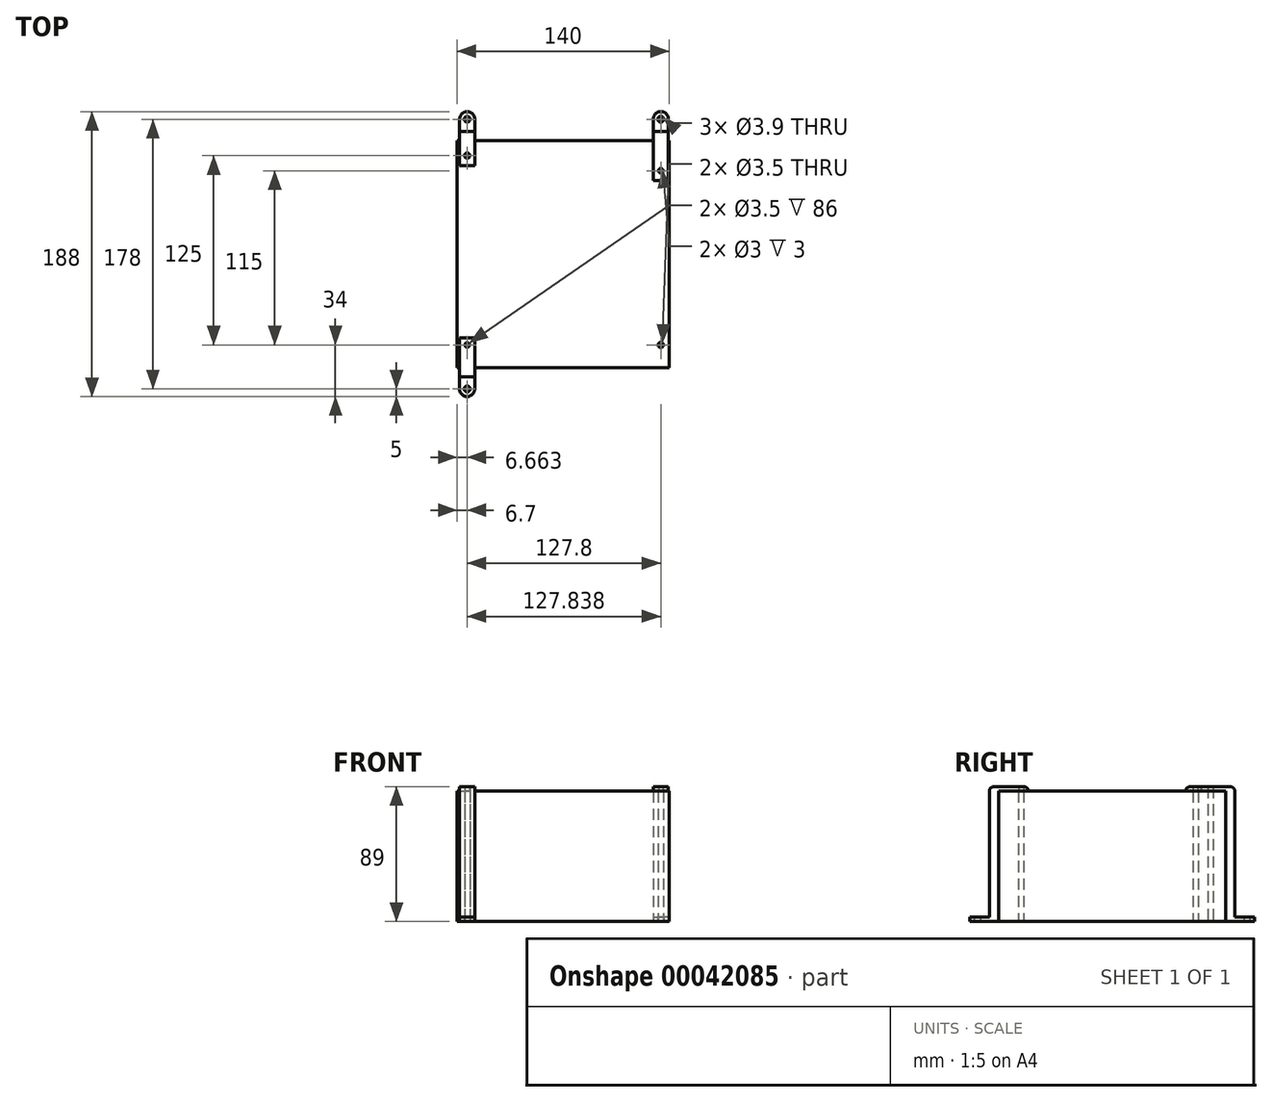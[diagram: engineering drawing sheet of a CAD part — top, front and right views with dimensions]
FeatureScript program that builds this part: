
annotation { "Feature Type Name" : "Feature", "Feature Type Description" : "" }
export const myFeature = defineFeature(function(context is Context, id is Id, definition is map)
    precondition{}
    {
        {
            var Q0;
            Q0=qCreatedBy(makeId("Top.planeOp"),FACE);
            var sketch = newSketch(context, id + "F0", { "sketchPlane" : qUnion([Q0])});
            skLineSegment(sketch, "E0.rect.bottom", {"start": v(70, -75) * mm, "end": v(-70, -75) * mm});
            skLineSegment(sketch, "E0.rect.top", {"start": v(70, 75) * mm, "end": v(-70, 75) * mm});
            skLineSegment(sketch, "E0.rect.left", {"start": v(70, -75) * mm, "end": v(70, 75) * mm});
            skLineSegment(sketch, "E0.rect.right", {"start": v(-70, -75) * mm, "end": v(-70, 75) * mm});
            skPoint(sketch, "E0.rect.middle", {"position": v(0, 0) * mm});
            skCircle(sketch, "E1", {"center": v(-63.3, 65) * mm, "radius": 1.75 * mm});
            skCircle(sketch, "E2", {"center": v(64.5, 55) * mm, "radius": 1.75 * mm});
            skCircle(sketch, "E3", {"center": v(64.5, -60) * mm, "radius": 1.75 * mm});
            skCircle(sketch, "E4", {"center": v(-63.3, -60) * mm, "radius": 1.75 * mm});
            skSolve(sketch);
        }
        {
            var Q0;
            Q0 = qSketchRegion(id + "F0", true);
            extrude(context, id + "F1", {"entities" : qUnion([Q0]), "depth" : 86 * mm});
        }
        {
            var Q0;
            Q0=qCreatedBy(makeId("Top.planeOp"),FACE);
            var sketch = newSketch(context, id + "F2", { "sketchPlane" : qUnion([Q0])});
            skCircle(sketch, "E5", {"center": v(-63.3, 89) * mm, "radius": 1.95 * mm});
            skCircle(sketch, "E6", {"center": v(-63.3, 89) * mm, "radius": 5 * mm});
            skLineSegment(sketch, "E7.bottom", {"start": v(-68.3, 75) * mm, "end": v(-58.3, 75) * mm});
            skLineSegment(sketch, "E7.top", {"start": v(-68.3, 81) * mm, "end": v(-58.3, 81) * mm});
            skLineSegment(sketch, "E7.left", {"start": v(-68.3, 75) * mm, "end": v(-68.3, 81) * mm});
            skLineSegment(sketch, "E7.right", {"start": v(-58.3, 75) * mm, "end": v(-58.3, 81) * mm});
            skLineSegment(sketch, "E8", {"start": v(-63.3, 98.83) * mm, "end": v(-63.3, 65) * mm, "construction": true});
            skLineSegment(sketch, "E9", {"start": v(-68.3, 81) * mm, "end": v(-68.3, 89) * mm});
            skLineSegment(sketch, "E10", {"start": v(-58.3, 81) * mm, "end": v(-58.3, 89) * mm});
            skSolve(sketch);
        }
        {
            var Q0;
            Q0=makeQuery(id+"F2.imprint","IMPRINT",FACE,{"disambiguationData":[TD([[makeQuery(id+"F2.imprint","IMPRINT",EDGE,{"derivedFrom":sQuery(id+"F2.wireOp",EDGE,"E5")}),-1.0]])]});
            var Q1;
            Q1=makeQuery(id+"F2.imprint","IMPRINT",FACE,{"disambiguationData":[TD([[makeQuery(id+"F2.imprint","IMPRINT",EDGE,{"derivedFrom":sQuery(id+"F2.wireOp",EDGE,"E7.top")}),1.0]])]});
            extrude(context, id + "F3", {"entities" : qUnion([Q0, Q1]), "depth" : 3 * mm});
        }
        {
            var Q0;
            Q0=makeQuery(id+"F2.imprint","IMPRINT",FACE,{"disambiguationData":[TD([[makeQuery(id+"F2.imprint","IMPRINT",EDGE,{"derivedFrom":sQuery(id+"F2.wireOp",EDGE,"E7.bottom")}),1.0]])]});
            extrude(context, id + "F4", {"entities" : qUnion([Q0]), "operationType" : NewBodyOperationType.ADD, "depth" : 86 * mm});
        }
        {
            var Q0;
            Q0=makeQuery(id+"F4.opExtrude","CAP_FACE",FACE,{"disambiguationData":[OSD([sQuery(id+"F2.wireOp",EDGE,"E7.bottom"),sQuery(id+"F2.wireOp",EDGE,"E7.top"),sQuery(id+"F2.wireOp",EDGE,"E7.left"),sQuery(id+"F2.wireOp",EDGE,"E7.right")])],"isStart":false});
            var sketch = newSketch(context, id + "F5", { "sketchPlane" : qUnion([Q0])});
            skLineSegment(sketch, "E11.bottom", {"start": v(-68.3, 81) * mm, "end": v(-58.3, 81) * mm});
            skLineSegment(sketch, "E11.top", {"start": v(-68.3, 58.38) * mm, "end": v(-58.3, 58.38) * mm});
            skLineSegment(sketch, "E11.left", {"start": v(-68.3, 81) * mm, "end": v(-68.3, 58.38) * mm});
            skLineSegment(sketch, "E11.right", {"start": v(-58.3, 81) * mm, "end": v(-58.3, 58.38) * mm});
            skCircle(sketch, "E12", {"center": v(-63.3, 65) * mm, "radius": 1.5 * mm});
            skSolve(sketch);
        }
        {
            var Q0;
            {var subQ2=sQuery(id+"F5.wireOp",EDGE,"E11.top");Q0=makeQuery(id+"F5.imprint","IMPRINT",FACE,{"disambiguationData":[TD([[makeQuery(id+"F5.imprint","IMPRINT",EDGE,{"derivedFrom":subQ2}),1.0]])]});}
            var Q1;
            {var subQ2=sQuery(id+"F5.wireOp",EDGE,"E11.bottom");Q1=makeQuery(id+"F5.imprint","IMPRINT",FACE,{"disambiguationData":[TD([[makeQuery(id+"F5.imprint","IMPRINT",EDGE,{"derivedFrom":subQ2}),-1.0]])]});}
            extrude(context, id + "F6", {"entities" : qUnion([Q0, Q1]), "operationType" : NewBodyOperationType.ADD, "depth" : 3 * mm});
        }
        {
            var Q0;
            Q0=qCreatedBy(makeId("Top.planeOp"),FACE);
            var sketch = newSketch(context, id + "F7", { "sketchPlane" : qUnion([Q0])});
            skCircle(sketch, "E13", {"center": v(64.5, 89) * mm, "radius": 1.95 * mm});
            skCircle(sketch, "E14", {"center": v(64.5, 89) * mm, "radius": 5 * mm});
            skLineSegment(sketch, "E15.bottom", {"start": v(59.5, 75) * mm, "end": v(69.5, 75) * mm});
            skLineSegment(sketch, "E15.top", {"start": v(59.5, 81) * mm, "end": v(69.5, 81) * mm});
            skLineSegment(sketch, "E15.left", {"start": v(59.5, 75) * mm, "end": v(59.5, 81) * mm});
            skLineSegment(sketch, "E15.right", {"start": v(69.5, 75) * mm, "end": v(69.5, 81) * mm});
            skLineSegment(sketch, "E16", {"start": v(64.5, 98.83) * mm, "end": v(64.5, 65) * mm, "construction": true});
            skLineSegment(sketch, "E17", {"start": v(59.5, 81) * mm, "end": v(59.5, 89) * mm});
            skLineSegment(sketch, "E18", {"start": v(69.5, 81) * mm, "end": v(69.5, 89) * mm});
            skSolve(sketch);
        }
        {
            var Q0;
            Q0=makeQuery(id+"F7.imprint","IMPRINT",FACE,{"disambiguationData":[TD([[makeQuery(id+"F7.imprint","IMPRINT",EDGE,{"derivedFrom":sQuery(id+"F7.wireOp",EDGE,"E13")}),-1.0]])]});
            var Q1;
            Q1=makeQuery(id+"F7.imprint","IMPRINT",FACE,{"disambiguationData":[TD([[makeQuery(id+"F7.imprint","IMPRINT",EDGE,{"derivedFrom":sQuery(id+"F7.wireOp",EDGE,"E15.top")}),1.0]])]});
            extrude(context, id + "F8", {"entities" : qUnion([Q0, Q1]), "depth" : 3 * mm});
        }
        {
            var Q0;
            Q0=makeQuery(id+"F7.imprint","IMPRINT",FACE,{"disambiguationData":[TD([[makeQuery(id+"F7.imprint","IMPRINT",EDGE,{"derivedFrom":sQuery(id+"F7.wireOp",EDGE,"E15.bottom")}),1.0]])]});
            extrude(context, id + "F9", {"entities" : qUnion([Q0]), "operationType" : NewBodyOperationType.ADD, "depth" : 86 * mm});
        }
        {
            var Q0;
            Q0=makeQuery(id+"F9.opExtrude","CAP_FACE",FACE,{"disambiguationData":[OSD([sQuery(id+"F7.wireOp",EDGE,"E15.bottom"),sQuery(id+"F7.wireOp",EDGE,"E15.top"),sQuery(id+"F7.wireOp",EDGE,"E15.left"),sQuery(id+"F7.wireOp",EDGE,"E15.right")])],"isStart":false});
            var sketch = newSketch(context, id + "F10", { "sketchPlane" : qUnion([Q0])});
            skLineSegment(sketch, "E19.bottom", {"start": v(59.5, 81) * mm, "end": v(69.5, 81) * mm});
            skLineSegment(sketch, "E19.top", {"start": v(59.5, 48.52) * mm, "end": v(69.5, 48.52) * mm});
            skLineSegment(sketch, "E19.left", {"start": v(59.5, 81) * mm, "end": v(59.5, 48.52) * mm});
            skLineSegment(sketch, "E19.right", {"start": v(69.5, 81) * mm, "end": v(69.5, 48.52) * mm});
            skCircle(sketch, "E20", {"center": v(64.5, 55) * mm, "radius": 1.5 * mm});
            skSolve(sketch);
        }
        {
            var Q0;
            Q0 = qSketchRegion(id + "F10", true);
            extrude(context, id + "F11", {"entities" : qUnion([Q0]), "operationType" : NewBodyOperationType.ADD, "depth" : 3 * mm});
        }
        {
            var Q0;
            Q0=qCreatedBy(makeId("Top.planeOp"),FACE);
            var sketch = newSketch(context, id + "F12", { "sketchPlane" : qUnion([Q0])});
            skCircle(sketch, "E21", {"center": v(-63.34, -89) * mm, "radius": 1.95 * mm});
            skCircle(sketch, "E22", {"center": v(-63.34, -89) * mm, "radius": 5 * mm});
            skLineSegment(sketch, "E23.bottom", {"start": v(-68.34, -75) * mm, "end": v(-58.34, -75) * mm});
            skLineSegment(sketch, "E23.top", {"start": v(-68.34, -81) * mm, "end": v(-58.34, -81) * mm});
            skLineSegment(sketch, "E23.left", {"start": v(-68.34, -81) * mm, "end": v(-68.34, -75) * mm});
            skLineSegment(sketch, "E23.right", {"start": v(-58.34, -81) * mm, "end": v(-58.34, -75) * mm});
            skLineSegment(sketch, "E24", {"start": v(-63.34, -31.67) * mm, "end": v(-63.34, -61.75) * mm, "construction": true});
            skLineSegment(sketch, "E25", {"start": v(-68.34, -89) * mm, "end": v(-68.34, -81) * mm});
            skLineSegment(sketch, "E26", {"start": v(-58.34, -89) * mm, "end": v(-58.34, -81) * mm});
            skSolve(sketch);
        }
        {
            var Q0;
            Q0=makeQuery(id+"F12.imprint","IMPRINT",FACE,{"disambiguationData":[TD([[makeQuery(id+"F12.imprint","IMPRINT",EDGE,{"derivedFrom":sQuery(id+"F12.wireOp",EDGE,"E23.bottom")}),-1.0]])]});
            extrude(context, id + "F13", {"entities" : qUnion([Q0]), "depth" : 86 * mm});
        }
        {
            var Q0;
            Q0=makeQuery(id+"F12.imprint","IMPRINT",FACE,{"disambiguationData":[TD([[makeQuery(id+"F12.imprint","IMPRINT",EDGE,{"derivedFrom":sQuery(id+"F12.wireOp",EDGE,"E23.top")}),-1.0]])]});
            var Q1;
            Q1=makeQuery(id+"F12.imprint","IMPRINT",FACE,{"disambiguationData":[TD([[makeQuery(id+"F12.imprint","IMPRINT",EDGE,{"derivedFrom":sQuery(id+"F12.wireOp",EDGE,"E21")}),-1.0]])]});
            extrude(context, id + "F14", {"entities" : qUnion([Q0, Q1]), "operationType" : NewBodyOperationType.ADD, "depth" : 3 * mm});
        }
        {
            var Q0;
            Q0=makeQuery(id+"F13.opExtrude","CAP_FACE",FACE,{"disambiguationData":[OSD([sQuery(id+"F12.wireOp",EDGE,"E23.bottom"),sQuery(id+"F12.wireOp",EDGE,"E23.top"),sQuery(id+"F12.wireOp",EDGE,"E23.left"),sQuery(id+"F12.wireOp",EDGE,"E23.right")])],"isStart":false});
            var sketch = newSketch(context, id + "F15", { "sketchPlane" : qUnion([Q0])});
            skLineSegment(sketch, "E27.bottom", {"start": v(-68.34, -55.23) * mm, "end": v(-58.34, -55.23) * mm});
            skLineSegment(sketch, "E27.top", {"start": v(-68.34, -81) * mm, "end": v(-58.34, -81) * mm});
            skLineSegment(sketch, "E27.left", {"start": v(-68.34, -55.23) * mm, "end": v(-68.34, -81) * mm});
            skLineSegment(sketch, "E27.right", {"start": v(-58.34, -55.23) * mm, "end": v(-58.34, -81) * mm});
            skCircle(sketch, "E28", {"center": v(-63.3, -60) * mm, "radius": 1.5 * mm});
            skSolve(sketch);
        }
        {
            var Q0;
            Q0 = qSketchRegion(id + "F15", true);
            extrude(context, id + "F16", {"entities" : qUnion([Q0]), "operationType" : NewBodyOperationType.ADD, "depth" : 3 * mm});
        }
        {
            var Q0;
            Q0=makeQuery(id+"F11.opExtrude","CAP_EDGE",EDGE,{"disambiguationData":[OSD([sQuery(id+"F10.wireOp",EDGE,"E19.bottom")])],"isStart":false});
            var Q1;
            Q1=makeQuery(id+"F6.opExtrude","CAP_EDGE",EDGE,{"disambiguationData":[OSD([sQuery(id+"F5.wireOp",EDGE,"E11.bottom")])],"isStart":false});
            var Q2;
            Q2=makeQuery(id+"F8.opExtrude","CAP_EDGE",EDGE,{"disambiguationData":[OSD([sQuery(id+"F7.wireOp",EDGE,"E15.top")])],"isStart":false});
            var Q3;
            Q3=makeQuery(id+"F3.opExtrude","CAP_EDGE",EDGE,{"disambiguationData":[OSD([sQuery(id+"F2.wireOp",EDGE,"E7.top")])],"isStart":false});
            var Q4;
            Q4=makeQuery(id+"F11.opExtrude","CAP_EDGE",EDGE,{"disambiguationData":[OSD([sQuery(id+"F10.wireOp",EDGE,"E19.top")])],"isStart":false});
            var Q5;
            Q5=makeQuery(id+"F6.opExtrude","CAP_EDGE",EDGE,{"disambiguationData":[OSD([sQuery(id+"F5.wireOp",EDGE,"E11.top")])],"isStart":false});
            var Q6;
            Q6=makeQuery(id+"F16.opExtrude","CAP_EDGE",EDGE,{"disambiguationData":[OSD([sQuery(id+"F15.wireOp",EDGE,"E27.top")])],"isStart":false});
            var Q7;
            Q7=makeQuery(id+"F16.opExtrude","CAP_EDGE",EDGE,{"disambiguationData":[OSD([sQuery(id+"F15.wireOp",EDGE,"E27.bottom")])],"isStart":false});
            var Q8;
            Q8=makeQuery(id+"F14.opExtrude","CAP_EDGE",EDGE,{"disambiguationData":[OSD([sQuery(id+"F12.wireOp",EDGE,"E23.top")])],"isStart":false});
            fillet(context, id + "F17", {"entities" : qUnion([Q0, Q1, Q2, Q3, Q4, Q5, Q6, Q7, Q8]), "radius" : 3 * mm, "tangentPropagation" : true, "allowEdgeOverflow" : false});
        }
    });
